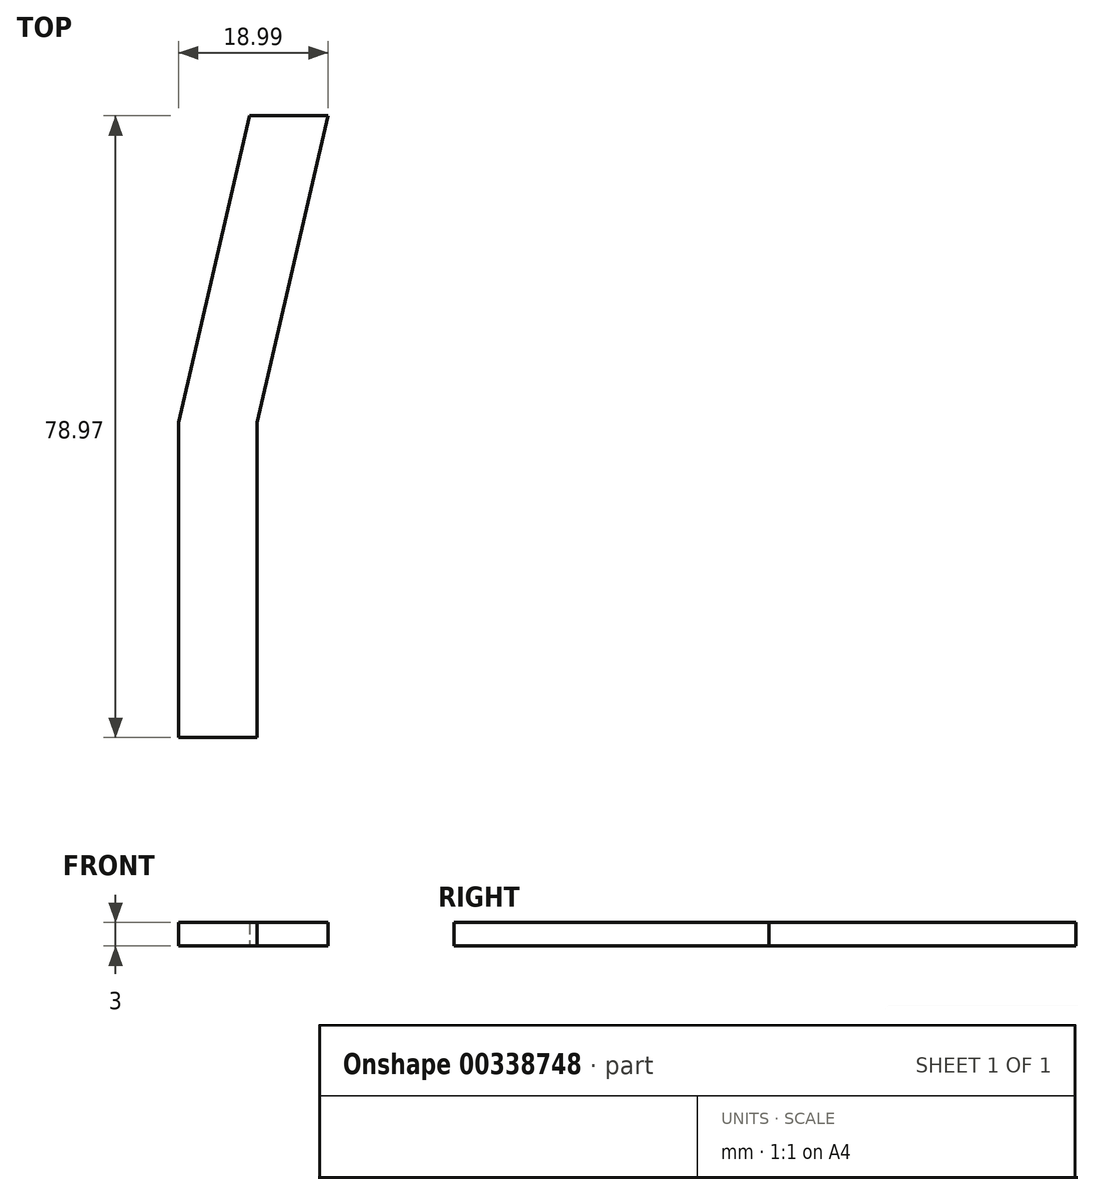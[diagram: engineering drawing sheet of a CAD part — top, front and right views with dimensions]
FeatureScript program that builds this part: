
annotation { "Feature Type Name" : "Feature", "Feature Type Description" : "" }
export const myFeature = defineFeature(function(context is Context, id is Id, definition is map)
    precondition{}
    {
        {
            var Q0;
            Q0=qCreatedBy(makeId("Top.planeOp"),FACE);
            var sketch = newSketch(context, id + "F0", { "sketchPlane" : qUnion([Q0])});
            skLineSegment(sketch, "E0", {"start": v(-28.6, -40) * mm, "end": v(-28.6, 0) * mm});
            skLineSegment(sketch, "E1", {"start": v(-28.6, 0) * mm, "end": v(-19.6, 38.97) * mm});
            skLineSegment(sketch, "E2", {"start": v(-19.6, 38.97) * mm, "end": v(-9.6, 38.97) * mm});
            skLineSegment(sketch, "E3", {"start": v(-9.6, 38.97) * mm, "end": v(-18.6, 0) * mm});
            skLineSegment(sketch, "E4", {"start": v(-18.6, 0) * mm, "end": v(-18.6, -40) * mm});
            skLineSegment(sketch, "E5", {"start": v(-18.6, -40) * mm, "end": v(-28.6, -40) * mm});
            skSolve(sketch);
        }
        {
            var Q0;
            Q0 = qSketchRegion(id + "F0", true);
            extrude(context, id + "F1", {"entities" : qUnion([Q0]), "depth" : 3 * mm});
        }
    });
